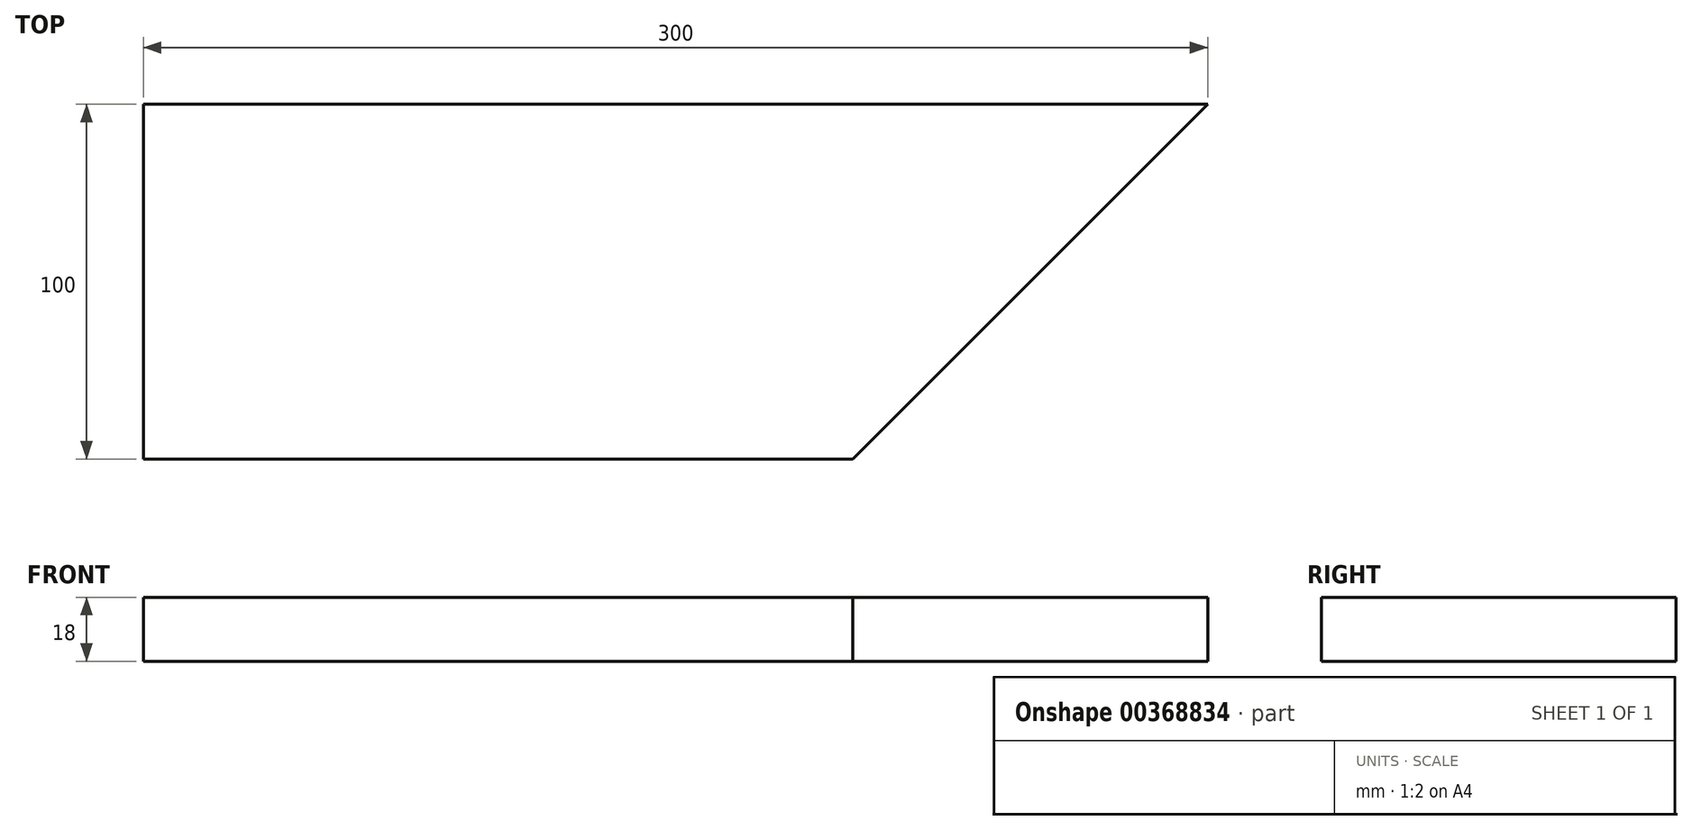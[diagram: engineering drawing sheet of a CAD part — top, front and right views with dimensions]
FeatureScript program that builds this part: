
annotation { "Feature Type Name" : "Feature", "Feature Type Description" : "" }
export const myFeature = defineFeature(function(context is Context, id is Id, definition is map)
    precondition{}
    {
        {
            var Q0;
            Q0=qCreatedBy(makeId("Top.planeOp"),FACE);
            var sketch = newSketch(context, id + "F0", { "sketchPlane" : qUnion([Q0])});
            skLineSegment(sketch, "E0", {"start": v(0, 0) * mm, "end": v(0, 100) * mm});
            skLineSegment(sketch, "E1", {"start": v(0, 100) * mm, "end": v(300, 100) * mm});
            skLineSegment(sketch, "E2", {"start": v(300, 100) * mm, "end": v(200, 0) * mm});
            skLineSegment(sketch, "E3", {"start": v(200, 0) * mm, "end": v(0, 0) * mm});
            skSolve(sketch);
        }
        {
            var Q0;
            Q0=makeQuery(id+"F0.imprint","IMPRINT",FACE,{"disambiguationData":[TD([[makeQuery(id+"F0.imprint","IMPRINT",EDGE,{"derivedFrom":sQuery(id+"F0.wireOp",EDGE,"E0")}),-1.0]])]});
            extrude(context, id + "F1", {"entities" : qUnion([Q0]), "depth" : 18 * mm});
        }
    });
